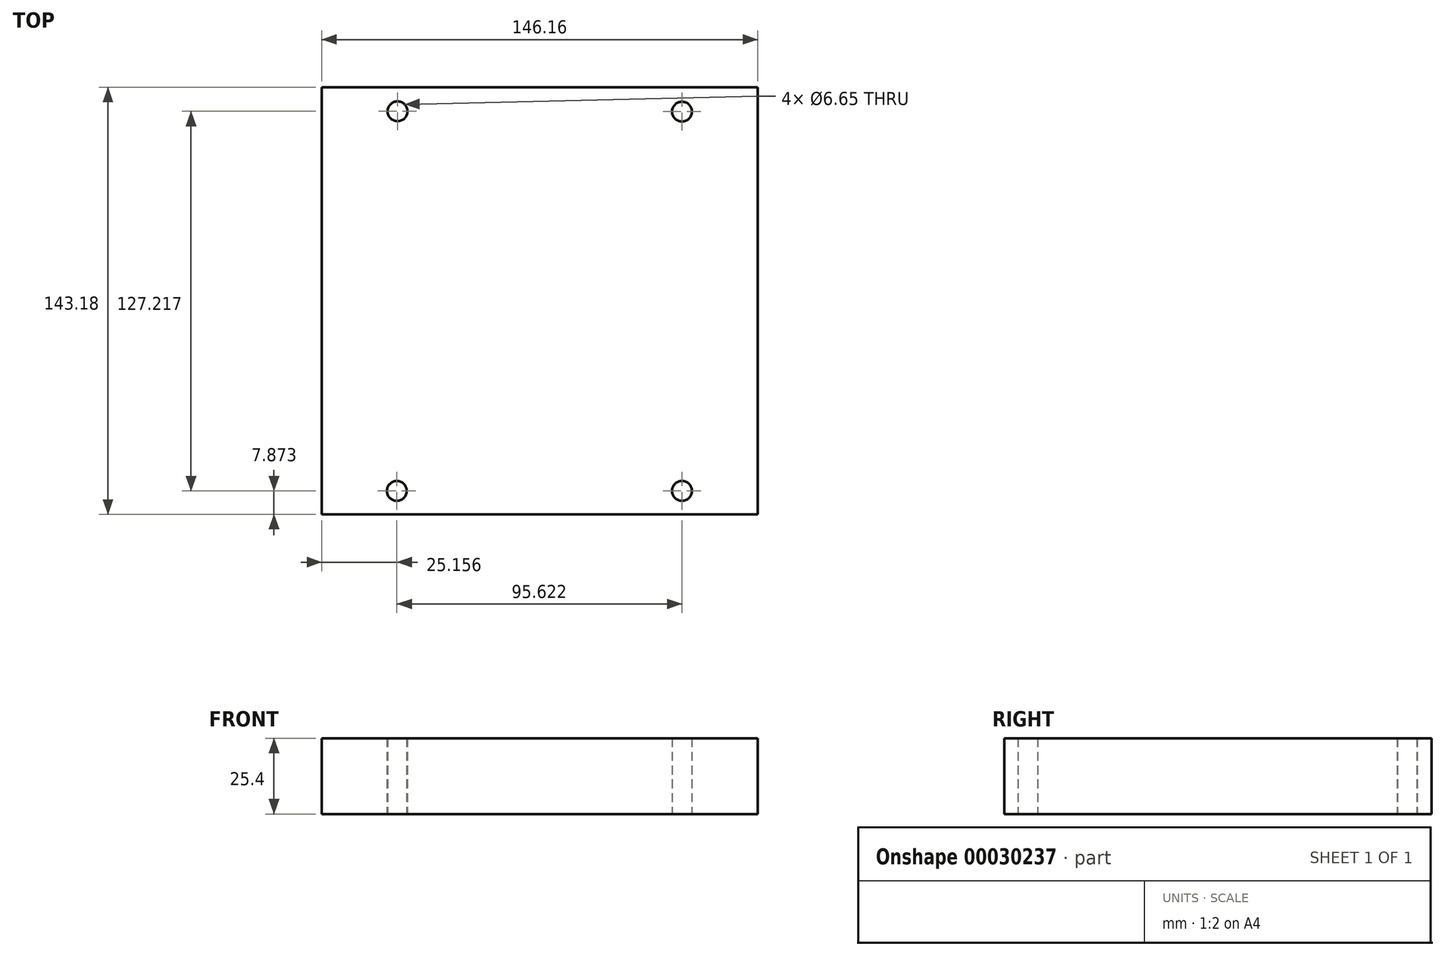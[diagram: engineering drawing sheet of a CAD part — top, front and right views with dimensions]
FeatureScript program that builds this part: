
annotation { "Feature Type Name" : "Feature", "Feature Type Description" : "" }
export const myFeature = defineFeature(function(context is Context, id is Id, definition is map)
    precondition{}
    {
        {
            var Q0;
            Q0=qCreatedBy(makeId("Top.planeOp"),FACE);
            var sketch = newSketch(context, id + "F0", { "sketchPlane" : qUnion([Q0])});
            skLineSegment(sketch, "E0.rect.bottom", {"start": v(73.08, 71.59) * mm, "end": v(-73.08, 71.59) * mm});
            skLineSegment(sketch, "E0.rect.top", {"start": v(73.08, -71.59) * mm, "end": v(-73.08, -71.59) * mm});
            skLineSegment(sketch, "E0.rect.left", {"start": v(73.08, 71.59) * mm, "end": v(73.08, -71.59) * mm});
            skLineSegment(sketch, "E0.rect.right", {"start": v(-73.08, 71.59) * mm, "end": v(-73.08, -71.59) * mm});
            skPoint(sketch, "E0.rect.middle", {"position": v(0, 0) * mm});
            skCircle(sketch, "E1", {"center": v(-47.68, 63.5) * mm, "radius": 3.32 * mm});
            skCircle(sketch, "E2", {"center": v(47.7, 63.4) * mm, "radius": 3.32 * mm});
            skCircle(sketch, "E3", {"center": v(-47.92, -63.72) * mm, "radius": 3.32 * mm});
            skCircle(sketch, "E4", {"center": v(47.7, -63.72) * mm, "radius": 3.32 * mm});
            skSolve(sketch);
        }
        {
            var Q0;
            Q0=makeQuery(id+"F0.imprint","IMPRINT",FACE,{"disambiguationData":[TD([[makeQuery(id+"F0.imprint","IMPRINT",EDGE,{"derivedFrom":sQuery(id+"F0.wireOp",EDGE,"E0.rect.bottom")}),1.0]])]});
            extrude(context, id + "F1", {"entities" : qUnion([Q0]), "depth" : 25.4 * mm});
        }
    });
